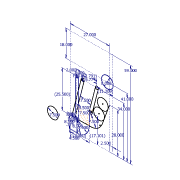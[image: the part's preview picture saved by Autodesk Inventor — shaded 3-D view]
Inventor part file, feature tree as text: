
AUTODESK INVENTOR PART (.ipt)
format: ipt  version: 2012 (Build 160160000, 160)  size: 102,912 bytes
history: native  units: in
note: dims shown in document units (in); Inventor stores cm internally (conversion verified against a paired STEP export)
features: sketch x1
ambient origin geometry x8: Origin, YZ Plane, XZ Plane, XY Plane, X Axis, Y Axis, Z Axis, Center Point
feature tree (1):
  sketch  "Sketch1"  dims[d3=8.5in d4=4.5in d5=0.375in d6=2.0in d7=7.5in d8=59.0in d9=27.0in d14=28.0in d15=13.0in d16=7.5in d17=18.0in d19=2.0in d21=7.5in d24=7.5in d26=1.0in d27=8.5in d28=1.0in d29=2.25in d30=7.5in d32=34.0in d33=8.0in d34=2.5in d36=11.2095in d37=41.0in d38=0.0in d39=13.7905in d40=9.7737in d41=4.0169in d42=25.5in d43=9.5in d44=17.1005in]
